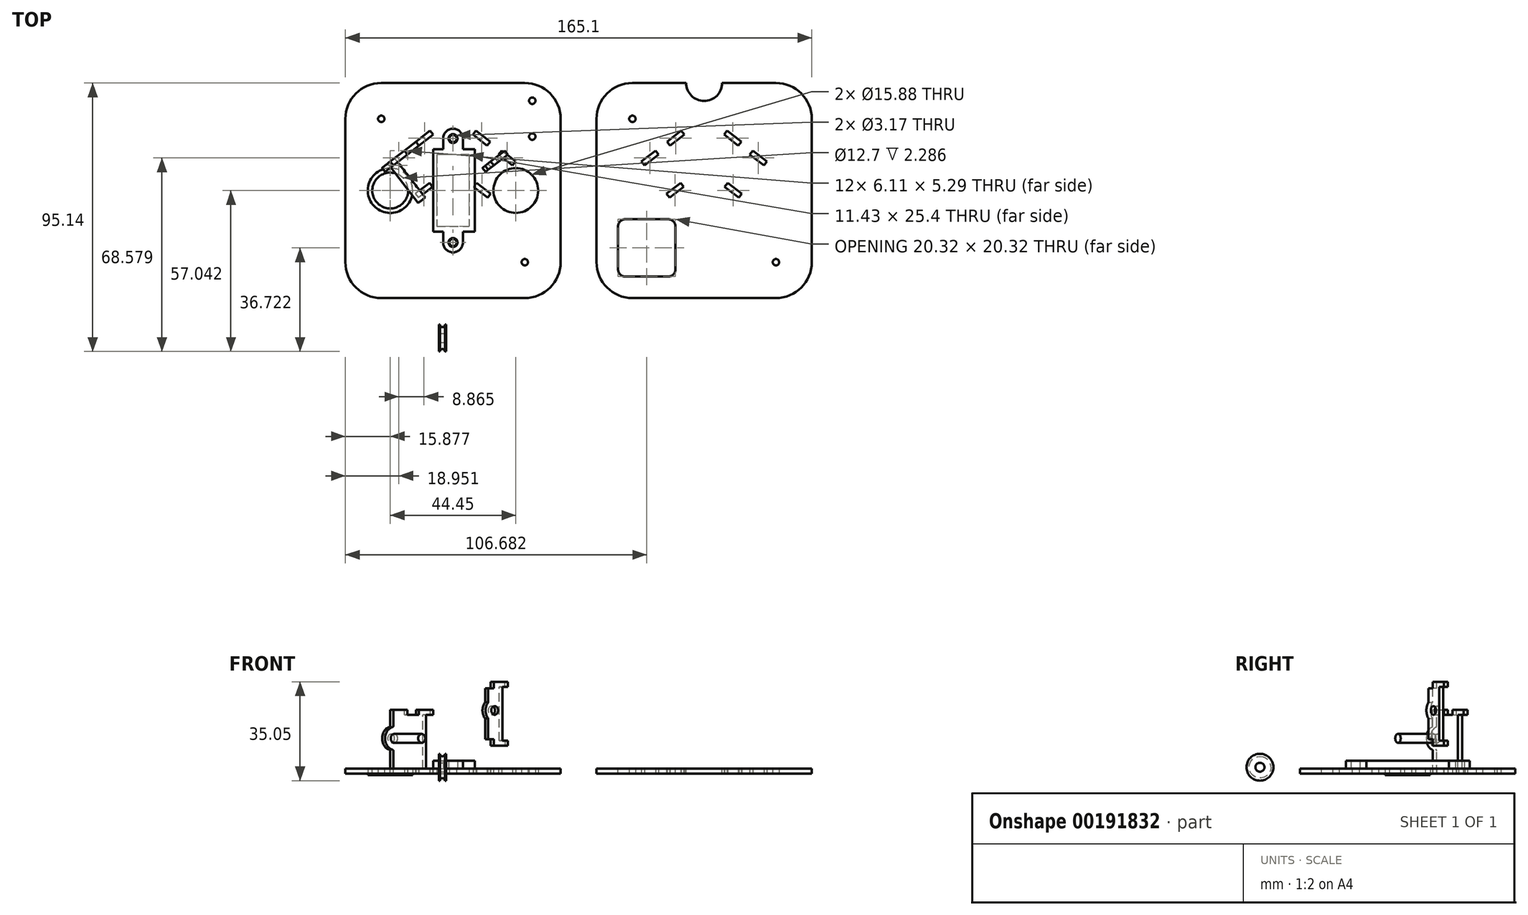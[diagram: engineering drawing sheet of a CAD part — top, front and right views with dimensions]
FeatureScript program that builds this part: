
annotation { "Feature Type Name" : "Feature", "Feature Type Description" : "" }
export const myFeature = defineFeature(function(context is Context, id is Id, definition is map)
    precondition{}
    {
        {
            var Q0;
            Q0=qCreatedBy(makeId("Top.planeOp"),FACE);
            var sketch = newSketch(context, id + "F0", { "sketchPlane" : qUnion([Q0])});
            skLineSegment(sketch, "E0.bottom", {"start": v(-22.88, 61.32) * mm, "end": v(27.92, 61.32) * mm});
            skLineSegment(sketch, "E0.top", {"start": v(-22.88, -14.88) * mm, "end": v(27.92, -14.88) * mm});
            skLineSegment(sketch, "E0.left", {"start": v(-35.58, 48.62) * mm, "end": v(-35.58, -2.18) * mm});
            skLineSegment(sketch, "E0.right", {"start": v(40.62, 48.62) * mm, "end": v(40.62, -2.18) * mm});
            skLineSegment(sketch, "E1", {"start": v(-35.58, 23.22) * mm, "end": v(-3.04, 23.22) * mm, "construction": true});
            skLineSegment(sketch, "E2", {"start": v(2.52, 61.32) * mm, "end": v(2.52, 35.92) * mm, "construction": true});
            skCircle(sketch, "E3", {"center": v(-19.7, 23.22) * mm, "radius": 7.94 * mm});
            skCircle(sketch, "E4.MirrorC", {"center": v(24.75, 23.22) * mm, "radius": 7.94 * mm});
            skLineSegment(sketch, "E5.left", {"start": v(-35.58, 25.46) * mm, "end": v(-35.58, 23.18) * mm});
            skLineSegment(sketch, "E5.right", {"start": v(40.62, 24.72) * mm, "end": v(40.62, 22.44) * mm});
            skPoint(sketch, "E6.visualSharp", {"position": v(-35.58, -14.88) * mm});
            skArc(sketch, "E6.filletArc", {"start": v(-35.58, -2.18) * mm, "mid": v(-31.86, -11.16) * mm, "end": v(-22.88, -14.88) * mm});
            skPoint(sketch, "E7.visualSharp", {"position": v(40.62, -14.88) * mm});
            skArc(sketch, "E7.filletArc", {"start": v(27.92, -14.88) * mm, "mid": v(36.9, -11.16) * mm, "end": v(40.62, -2.18) * mm});
            skPoint(sketch, "E8.visualSharp", {"position": v(40.62, 61.32) * mm});
            skArc(sketch, "E8.filletArc", {"start": v(40.62, 48.62) * mm, "mid": v(36.9, 57.6) * mm, "end": v(27.92, 61.32) * mm});
            skPoint(sketch, "E9.visualSharp", {"position": v(-35.58, 61.32) * mm});
            skArc(sketch, "E9.filletArc", {"start": v(-22.88, 61.32) * mm, "mid": v(-31.86, 57.6) * mm, "end": v(-35.58, 48.62) * mm});
            skLineSegment(sketch, "E10.top", {"start": v(2.52, 35.92) * mm, "end": v(-3.2, 35.92) * mm});
            skLineSegment(sketch, "E11.trimOffspring", {"start": v(8.09, 23.22) * mm, "end": v(40.62, 23.22) * mm, "construction": true});
            skLineSegment(sketch, "E12.trimOffspring", {"start": v(2.52, 10.52) * mm, "end": v(2.52, -14.88) * mm, "construction": true});
            skLineSegment(sketch, "E13.MirrorCS", {"start": v(2.52, 10.52) * mm, "end": v(-3.2, 10.52) * mm});
            skLineSegment(sketch, "E14.MirrorCS", {"start": v(2.52, 10.52) * mm, "end": v(8.24, 10.52) * mm});
            skLineSegment(sketch, "E15.MirrorCS", {"start": v(2.52, 35.92) * mm, "end": v(8.24, 35.92) * mm});
            skLineSegment(sketch, "E16.bottom", {"start": v(-3.2, 35.92) * mm, "end": v(3.3, 35.92) * mm});
            skLineSegment(sketch, "E16.top", {"start": v(-3.2, 10.52) * mm, "end": v(2.52, 10.52) * mm});
            skLineSegment(sketch, "E16.left", {"start": v(-3.2, 35.92) * mm, "end": v(-3.2, 10.52) * mm});
            skPoint(sketch, "E16.right.start.orphan", {"position": v(2.52, 23.22) * mm});
            skCircle(sketch, "E17", {"center": v(2.52, 41.64) * mm, "radius": 1.27 * mm});
            skCircle(sketch, "E18.MirrorC", {"center": v(2.52, 4.8) * mm, "radius": 1.27 * mm});
            skLineSegment(sketch, "E19.MirrorCS", {"start": v(8.24, 35.92) * mm, "end": v(8.24, 10.52) * mm});
            skLineSegment(sketch, "E20", {"start": v(-13.43, 28.08) * mm, "end": v(3.77, 41.4) * mm, "construction": true});
            skLineSegment(sketch, "E21.0", {"start": v(-12.05, 21.12) * mm, "end": v(-3.2, 27.98) * mm, "construction": true});
            skLineSegment(sketch, "E22", {"start": v(-13.57, 36) * mm, "end": v(-14.66, 37.4) * mm});
            skLineSegment(sketch, "E23", {"start": v(-14.66, 37.4) * mm, "end": v(-19.68, 33.52) * mm});
            skLineSegment(sketch, "E24", {"start": v(-10.63, 36.35) * mm, "end": v(-7.68, 32.53) * mm, "construction": true});
            skLineSegment(sketch, "E25", {"start": v(-13.57, 36) * mm, "end": v(-18.6, 32.11) * mm});
            skLineSegment(sketch, "E26", {"start": v(-18.6, 32.11) * mm, "end": v(-19.68, 33.52) * mm});
            skLineSegment(sketch, "E27.MirrorCS", {"start": v(-9.56, 39.11) * mm, "end": v(-10.65, 40.52) * mm});
            skLineSegment(sketch, "E28.MirrorCS", {"start": v(-9.56, 39.11) * mm, "end": v(-4.54, 43) * mm});
            skLineSegment(sketch, "E29.MirrorCS", {"start": v(-10.65, 40.52) * mm, "end": v(-5.63, 44.4) * mm});
            skLineSegment(sketch, "E30.MirrorCS", {"start": v(-4.54, 43) * mm, "end": v(-5.63, 44.4) * mm});
            skLineSegment(sketch, "E31.MirrorCS", {"start": v(-5.8, 25.96) * mm, "end": v(-10.82, 22.07) * mm});
            skLineSegment(sketch, "E32.MirrorCS", {"start": v(-4.7, 24.55) * mm, "end": v(-9.73, 20.67) * mm});
            skLineSegment(sketch, "E33.MirrorCS", {"start": v(-10.82, 22.07) * mm, "end": v(-9.73, 20.67) * mm});
            skLineSegment(sketch, "E34.MirrorCS", {"start": v(-5.8, 25.96) * mm, "end": v(-4.7, 24.55) * mm});
            skLineSegment(sketch, "E35.MirrorCS", {"start": v(18.62, 36) * mm, "end": v(23.64, 32.11) * mm});
            skLineSegment(sketch, "E36.MirrorCS", {"start": v(23.64, 32.11) * mm, "end": v(24.73, 33.52) * mm});
            skLineSegment(sketch, "E37.MirrorCS", {"start": v(19.7, 37.4) * mm, "end": v(24.73, 33.52) * mm});
            skLineSegment(sketch, "E38.MirrorCS", {"start": v(18.62, 36) * mm, "end": v(19.7, 37.4) * mm});
            skLineSegment(sketch, "E39.MirrorCS", {"start": v(9.75, 24.55) * mm, "end": v(14.77, 20.67) * mm});
            skLineSegment(sketch, "E40.MirrorCS", {"start": v(10.84, 25.96) * mm, "end": v(9.75, 24.55) * mm});
            skLineSegment(sketch, "E41.MirrorCS", {"start": v(15.86, 22.07) * mm, "end": v(14.77, 20.67) * mm});
            skLineSegment(sketch, "E42.MirrorCS", {"start": v(17.1, 21.12) * mm, "end": v(8.24, 27.98) * mm, "construction": true});
            skLineSegment(sketch, "E43.MirrorCS", {"start": v(14.6, 39.11) * mm, "end": v(9.58, 43) * mm});
            skLineSegment(sketch, "E44.MirrorCS", {"start": v(9.58, 43) * mm, "end": v(10.67, 44.4) * mm});
            skLineSegment(sketch, "E45.MirrorCS", {"start": v(14.6, 39.11) * mm, "end": v(15.7, 40.52) * mm});
            skLineSegment(sketch, "E46.MirrorCS", {"start": v(15.7, 40.52) * mm, "end": v(10.67, 44.4) * mm});
            skLineSegment(sketch, "E47", {"start": v(10.84, 25.96) * mm, "end": v(15.86, 22.07) * mm});
            skLineSegment(sketch, "E48", {"start": v(12.1, 41.05) * mm, "end": v(13.18, 42.46) * mm, "construction": true});
            skCircle(sketch, "E49", {"center": v(30.58, 42.33) * mm, "radius": 1.14 * mm});
            skCircle(sketch, "E50", {"center": v(30.58, 55.03) * mm, "radius": 1.14 * mm});
            skCircle(sketch, "E51", {"center": v(27.92, -2.18) * mm, "radius": 1.13 * mm});
            skCircle(sketch, "E52", {"center": v(-22.88, 48.62) * mm, "radius": 1.14 * mm});
            skSolve(sketch);
        }
        {
            var Q0;
            Q0=makeQuery(id+"F0.imprint","IMPRINT",FACE,{"disambiguationData":[TD([[makeQuery(id+"F0.imprint","IMPRINT",EDGE,{"derivedFrom":sQuery(id+"F0.wireOp",EDGE,"E0.bottom")}),-1.0]])]});
            extrude(context, id + "F1", {"entities" : qUnion([Q0]), "depth" : 1.78 * mm});
        }
        {
            var Q0;
            Q0=makeQuery(id+"F1.opExtrude","SWEPT_FACE",FACE,{"disambiguationData":[OSD([sQuery(id+"F0.wireOp",EDGE,"E23")])]});
            var sketch = newSketch(context, id + "F2", { "sketchPlane" : qUnion([Q0])});
            skLineSegment(sketch, "E53.top", {"start": v(16.4, 20.83) * mm, "end": v(16.4, 20.83) * mm});
            skCircle(sketch, "E54", {"center": v(5.34, 12.45) * mm, "radius": 1.52 * mm});
            skLineSegment(sketch, "E55", {"start": v(4.96, 2.29) * mm, "end": v(4.96, 7.96) * mm});
            skPoint(sketch, "E53.left.start.orphan", {"position": v(-28.95, 2.29) * mm});
            skPoint(sketch, "E56.orphan", {"position": v(-15.62, 20.83) * mm});
            skPoint(sketch, "E53.right.end.orphan", {"position": v(60.58, 20.83) * mm});
            skPoint(sketch, "E53.right.start.orphan", {"position": v(73.92, 2.29) * mm});
            skLineSegment(sketch, "E57", {"start": v(5.27, 11.3) * mm, "end": v(13.84, 11.3) * mm, "construction": true});
            skLineSegment(sketch, "E58.MirrorCS", {"start": v(4.96, 22.6) * mm, "end": v(11.31, 22.6) * mm});
            skLineSegment(sketch, "E59.MirrorCS", {"start": v(11.31, 20.83) * mm, "end": v(11.31, 22.6) * mm});
            skArc(sketch, "E60.0", {"start": v(4.55, 16.43) * mm, "mid": v(1.28, 12.45) * mm, "end": v(4.55, 8.46) * mm});
            skPoint(sketch, "E61.visualSharp", {"position": v(4.96, 16.5) * mm});
            skArc(sketch, "E61.filletArc", {"start": v(4.55, 16.43) * mm, "mid": v(4.85, 16.6) * mm, "end": v(4.96, 16.93) * mm});
            skPoint(sketch, "E62.visualSharp", {"position": v(4.96, 8.4) * mm});
            skArc(sketch, "E62.filletArc", {"start": v(4.96, 7.96) * mm, "mid": v(4.85, 8.28) * mm, "end": v(4.55, 8.46) * mm});
            skLineSegment(sketch, "E63.MirrorCS", {"start": v(11.31, 20.83) * mm, "end": v(16.4, 20.83) * mm});
            skPoint(sketch, "E64.top.start.orphan", {"position": v(22.48, 6.1) * mm});
            skLineSegment(sketch, "E65", {"start": v(11.31, 1.78) * mm, "end": v(16.4, 1.78) * mm});
            skLineSegment(sketch, "E66.top", {"start": v(22.74, 0) * mm, "end": v(16.4, 0) * mm});
            skLineSegment(sketch, "E66.right", {"start": v(16.4, 1.78) * mm, "end": v(16.4, 0) * mm});
            skLineSegment(sketch, "E67.MirrorCS", {"start": v(22.74, 22.6) * mm, "end": v(16.4, 22.6) * mm});
            skLineSegment(sketch, "E68.MirrorCS", {"start": v(16.4, 20.83) * mm, "end": v(16.4, 22.6) * mm});
            skLineSegment(sketch, "E69.top", {"start": v(11.31, 0) * mm, "end": v(4.96, 0) * mm});
            skLineSegment(sketch, "E69.left", {"start": v(11.31, 1.78) * mm, "end": v(11.31, 0) * mm});
            skLineSegment(sketch, "E69.right", {"start": v(4.96, 2.29) * mm, "end": v(4.96, 0) * mm});
            skLineSegment(sketch, "E70", {"start": v(4.96, 16.93) * mm, "end": v(4.96, 22.6) * mm});
            skLineSegment(sketch, "E71", {"start": v(22.74, 22.6) * mm, "end": v(22.74, 20.83) * mm});
            skLineSegment(sketch, "E72.bottom", {"start": v(22.74, 1.78) * mm, "end": v(19.57, 1.78) * mm});
            skLineSegment(sketch, "E72.top", {"start": v(22.74, 20.83) * mm, "end": v(19.57, 20.83) * mm});
            skLineSegment(sketch, "E72.right", {"start": v(19.57, 1.78) * mm, "end": v(19.57, 20.83) * mm});
            skLineSegment(sketch, "E73.trimOffspring", {"start": v(22.74, 1.78) * mm, "end": v(22.74, 0) * mm});
            skSolve(sketch);
        }
        {
            var Q0;
            Q0=makeQuery(id+"F2.imprint","IMPRINT",FACE,{"disambiguationData":[TD([[makeQuery(id+"F2.imprint","IMPRINT",EDGE,{"derivedFrom":sQuery(id+"F2.wireOp",EDGE,"E54")}),-1.0]])]});
            var Q1;
            Q1=makeQuery(id+"F2.imprint","IMPRINT",FACE,{"disambiguationData":[TD([[makeQuery(id+"F2.imprint","IMPRINT",EDGE,{"derivedFrom":sQuery(id+"F2.wireOp",EDGE,"E69.top")}),-1.0]])]});
            extrude(context, id + "F3", {"entities" : qUnion([Q0, Q1]), "depth" : 1.78 * mm});
        }
        {
            var Q0;
            Q0=makeQuery(id+"F3.opExtrude","SWEPT_BODY",BODY,{"disambiguationData":[OSD([sQuery(id+"F2.wireOp",EDGE,"E53.bottom"),sQuery(id+"F2.wireOp",EDGE,"E53.top"),sQuery(id+"F2.wireOp",EDGE,"E54"),sQuery(id+"F2.wireOp",EDGE,"39a69e0f-4cb4-4542-a178-ce5a3710d4660.MirrorCS"),sQuery(id+"F2.wireOp",EDGE,"5af08400-f977-49c8-b0c8-0518a07f6a520.MirrorCS"),sQuery(id+"F2.wireOp",EDGE,"84274afa-9e7b-4732-9adf-5b7f6b23458d0.MirrorCS"),sQuery(id+"F2.wireOp",EDGE,"E55"),sQuery(id+"F2.wireOp",EDGE,"e57e3ef5-8313-4936-b405-59ef127ed5260.MirrorCS"),sQuery(id+"F2.wireOp",EDGE,"d303f1ce-a37b-40ea-9413-96a8a4c887890.MirrorC"),sQuery(id+"F2.wireOp",EDGE,"Hnc1nS2l-cVDs-HAgH-h4le-MnPWrZNVOkKI.top"),sQuery(id+"F2.wireOp",EDGE,"Hnc1nS2l-cVDs-HAgH-h4le-MnPWrZNVOkKI.left"),sQuery(id+"F2.wireOp",EDGE,"Hnc1nS2l-cVDs-HAgH-h4le-MnPWrZNVOkKI.right"),sQuery(id+"F2.wireOp",EDGE,"d3e6619f-e4b7-4664-bd97-2753edbc48ab0.MirrorCS"),sQuery(id+"F2.wireOp",EDGE,"cd9f6806-109e-4446-bf17-cb16760e91a50.MirrorCS"),sQuery(id+"F2.wireOp",EDGE,"0c942e14-5766-4280-9eae-b5e6824674920.MirrorCS"),sQuery(id+"F2.wireOp",EDGE,"PotOPIpM-QwAl-Cd0Z-i22J-7vAqHJB9KxQS.top"),sQuery(id+"F2.wireOp",EDGE,"PotOPIpM-QwAl-Cd0Z-i22J-7vAqHJB9KxQS.left"),sQuery(id+"F2.wireOp",EDGE,"PotOPIpM-QwAl-Cd0Z-i22J-7vAqHJB9KxQS.right")])]});
            transform(context, id + "F4", {"entities" : qUnion([Q0]), "transformType" : TransformType.TRANSLATION_3D, "dx" : 0 * mm, "dy" : -13.97 * mm, "dz" : 0 * mm, "makeCopy" : true});
        }
        {
            var Q0;
            Q0=qCreatedBy(makeId("Top.planeOp"),FACE);
            var sketch = newSketch(context, id + "F5", { "sketchPlane" : qUnion([Q0])});
            skLineSegment(sketch, "E74.bottom", {"start": v(-11.14, -35.94) * mm, "end": v(-8.6, -35.94) * mm});
            skLineSegment(sketch, "E74.top", {"start": v(-11.14, -31.18) * mm, "end": v(-10.76, -31.18) * mm});
            skLineSegment(sketch, "E74.left", {"start": v(-11.14, -35.94) * mm, "end": v(-11.14, -31.18) * mm});
            skLineSegment(sketch, "E74.right", {"start": v(-8.6, -35.94) * mm, "end": v(-8.6, -31.18) * mm});
            skArc(sketch, "E75", {"start": v(-10.76, -31.18) * mm, "mid": v(-9.87, -32.07) * mm, "end": v(-8.98, -31.18) * mm});
            skLineSegment(sketch, "E76.trimOffspring", {"start": v(-8.98, -31.18) * mm, "end": v(-8.6, -31.18) * mm});
            skSolve(sketch);
        }
        {
            var Q0;
            Q0 = qSketchRegion(id + "F5", true);
            var Q1;
            Q1=sQuery(id+"F5.wireOp",EDGE,"E74.bottom");
            revolve(context, id + "F6", {"entities" : qUnion([Q0]), "axis" : qUnion([Q1]), "revolveType" : RevolveType.FULL});
        }
        {
            var Q0;
            Q0=makeQuery(id+"F6.opRevolve","SWEPT_FACE",FACE,{"disambiguationData":[OSD([sQuery(id+"F5.wireOp",EDGE,"E74.right")])]});
            var sketch = newSketch(context, id + "F7", { "sketchPlane" : qUnion([Q0])});
            skCircle(sketch, "E77", {"center": v(-35.94, 0) * mm, "radius": 1.59 * mm});
            skSolve(sketch);
        }
        {
            var Q0;
            Q0 = qSketchRegion(id + "F7", true);
            extrude(context, id + "F8", {"entities" : qUnion([Q0]), "operationType" : NewBodyOperationType.REMOVE, "endBound" : BoundingType.THROUGH_ALL, "oppositeDirection" : true, "depth" : 25.4 * mm});
        }
        {
            var Q0;
            Q0=makeQuery(id+"F6.opRevolve","SWEPT_BODY",BODY,{"disambiguationData":[OSD([sQuery(id+"F5.wireOp",EDGE,"E74.bottom"),sQuery(id+"F5.wireOp",EDGE,"E74.top"),sQuery(id+"F5.wireOp",EDGE,"E74.left"),sQuery(id+"F5.wireOp",EDGE,"E74.right"),sQuery(id+"F5.wireOp",EDGE,"E75"),sQuery(id+"F5.wireOp",EDGE,"E76.trimOffspring")])]});
            transform(context, id + "F9", {"entities" : qUnion([Q0]), "transformType" : TransformType.TRANSLATION_3D, "dx" : 8.64 * mm, "dy" : 6.88 * mm, "dz" : -0.32 * mm, "makeCopy" : false});
        }
        {
            var Q0;
            Q0=makeQuery(id+"F6.opRevolve","SWEPT_BODY",BODY,{"disambiguationData":[OSD([sQuery(id+"F5.wireOp",EDGE,"E74.bottom"),sQuery(id+"F5.wireOp",EDGE,"E74.top"),sQuery(id+"F5.wireOp",EDGE,"E74.left"),sQuery(id+"F5.wireOp",EDGE,"E74.right"),sQuery(id+"F5.wireOp",EDGE,"E75"),sQuery(id+"F5.wireOp",EDGE,"E76.trimOffspring")])]});
            transform(context, id + "F10", {"entities" : qUnion([Q0]), "transformType" : TransformType.TRANSLATION_3D, "dx" : 33.53 * mm, "dy" : 0 * mm, "dz" : 0 * mm, "makeCopy" : true});
        }
        {
            var Q0;
            Q0=makeQuery(id+"F4.opPattern","COPY",BODY,{"derivedFrom":makeQuery(id+"F3.opExtrude","SWEPT_BODY",BODY,{"disambiguationData":[OSD([sQuery(id+"F2.wireOp",EDGE,"E53.bottom"),sQuery(id+"F2.wireOp",EDGE,"E53.top"),sQuery(id+"F2.wireOp",EDGE,"E54"),sQuery(id+"F2.wireOp",EDGE,"39a69e0f-4cb4-4542-a178-ce5a3710d4660.MirrorCS"),sQuery(id+"F2.wireOp",EDGE,"5af08400-f977-49c8-b0c8-0518a07f6a520.MirrorCS"),sQuery(id+"F2.wireOp",EDGE,"84274afa-9e7b-4732-9adf-5b7f6b23458d0.MirrorCS"),sQuery(id+"F2.wireOp",EDGE,"E55"),sQuery(id+"F2.wireOp",EDGE,"e57e3ef5-8313-4936-b405-59ef127ed5260.MirrorCS"),sQuery(id+"F2.wireOp",EDGE,"d303f1ce-a37b-40ea-9413-96a8a4c887890.MirrorC"),sQuery(id+"F2.wireOp",EDGE,"Hnc1nS2l-cVDs-HAgH-h4le-MnPWrZNVOkKI.top"),sQuery(id+"F2.wireOp",EDGE,"Hnc1nS2l-cVDs-HAgH-h4le-MnPWrZNVOkKI.left"),sQuery(id+"F2.wireOp",EDGE,"Hnc1nS2l-cVDs-HAgH-h4le-MnPWrZNVOkKI.right"),sQuery(id+"F2.wireOp",EDGE,"d3e6619f-e4b7-4664-bd97-2753edbc48ab0.MirrorCS"),sQuery(id+"F2.wireOp",EDGE,"cd9f6806-109e-4446-bf17-cb16760e91a50.MirrorCS"),sQuery(id+"F2.wireOp",EDGE,"0c942e14-5766-4280-9eae-b5e6824674920.MirrorCS"),sQuery(id+"F2.wireOp",EDGE,"PotOPIpM-QwAl-Cd0Z-i22J-7vAqHJB9KxQS.top"),sQuery(id+"F2.wireOp",EDGE,"PotOPIpM-QwAl-Cd0Z-i22J-7vAqHJB9KxQS.left"),sQuery(id+"F2.wireOp",EDGE,"PotOPIpM-QwAl-Cd0Z-i22J-7vAqHJB9KxQS.right")])]}),"instanceName":"1"});
            var Q1;
            Q1=makeQuery(id+"F5I5v5MRCHO6jwp_3.opPattern","COPY",BODY,{"derivedFrom":makeQuery(id+"FqVhxczo7vmOwjE_2.opExtrude","SWEPT_BODY",BODY,{"disambiguationData":[OSD([sQuery(id+"Ffx07k7tmxWMfFj_2.wireOp",EDGE,"6cq6P109-h6eB-oaLu-sk0c-LIsEAzt6sABo")])]}),"instanceName":"1"});
            deleteBodies(context, id + "F11", {"entities" : qUnion([Q0, Q1])});
        }
        {
            var Q0;
            Q0=makeQuery(id+"F10.opPattern","COPY",BODY,{"derivedFrom":makeQuery(id+"F6.opRevolve","SWEPT_BODY",BODY,{"disambiguationData":[OSD([sQuery(id+"F5.wireOp",EDGE,"E74.bottom"),sQuery(id+"F5.wireOp",EDGE,"E74.top"),sQuery(id+"F5.wireOp",EDGE,"E74.left"),sQuery(id+"F5.wireOp",EDGE,"E74.right"),sQuery(id+"F5.wireOp",EDGE,"E75"),sQuery(id+"F5.wireOp",EDGE,"E76.trimOffspring")])]}),"instanceName":"1"});
            deleteBodies(context, id + "F12", {"entities" : qUnion([Q0])});
        }
        {
            var Q0;
            Q0=makeQuery(id+"F6.opRevolve","SWEPT_BODY",BODY,{"disambiguationData":[OSD([sQuery(id+"F5.wireOp",EDGE,"E74.bottom"),sQuery(id+"F5.wireOp",EDGE,"E74.top"),sQuery(id+"F5.wireOp",EDGE,"E74.left"),sQuery(id+"F5.wireOp",EDGE,"E74.right"),sQuery(id+"F5.wireOp",EDGE,"E75"),sQuery(id+"F5.wireOp",EDGE,"E76.trimOffspring")])]});
            transform(context, id + "F13", {"entities" : qUnion([Q0]), "transformType" : TransformType.TRANSLATION_3D, "dx" : 0 * mm, "dy" : 0 * mm, "dz" : 2.54 * mm, "makeCopy" : false});
        }
        {
            var Q0;
            Q0=makeQuery(id+"F1.opExtrude","CAP_FACE",FACE,{"disambiguationData":[OSD([sQuery(id+"F0.wireOp",EDGE,"E0.bottom"),sQuery(id+"F0.wireOp",EDGE,"E0.top"),sQuery(id+"F0.wireOp",EDGE,"E0.left"),sQuery(id+"F0.wireOp",EDGE,"E0.right"),sQuery(id+"F0.wireOp",EDGE,"E3"),sQuery(id+"F0.wireOp",EDGE,"E4.MirrorC"),sQuery(id+"F0.wireOp",EDGE,"E5.left"),sQuery(id+"F0.wireOp",EDGE,"E5.right"),sQuery(id+"F0.wireOp",EDGE,"1d3f4JpI-8B3J-cx4F-wrh8-YEHR3C14XcvI.bottom"),sQuery(id+"F0.wireOp",EDGE,"1d3f4JpI-8B3J-cx4F-wrh8-YEHR3C14XcvI.top"),sQuery(id+"F0.wireOp",EDGE,"1d3f4JpI-8B3J-cx4F-wrh8-YEHR3C14XcvI.left"),sQuery(id+"F0.wireOp",EDGE,"1d3f4JpI-8B3J-cx4F-wrh8-YEHR3C14XcvI.right"),sQuery(id+"F0.wireOp",EDGE,"ded24c36-2829-4a26-ae88-f7eb7b782ba40.MirrorCS"),sQuery(id+"F0.wireOp",EDGE,"0885069f-9e6d-484d-b19d-ad6ea1b2afb20.MirrorCS"),sQuery(id+"F0.wireOp",EDGE,"d2e7fe8c-65ad-4f29-82e6-2e3cbba0d0cb0.MirrorCS"),sQuery(id+"F0.wireOp",EDGE,"fc1c7216-331c-41ae-9cee-ffb66b4a45bf0.MirrorCS"),sQuery(id+"F0.wireOp",EDGE,"71281703-b980-4b41-ad92-6ab3323842a52.MirrorCS"),sQuery(id+"F0.wireOp",EDGE,"71281703-b980-4b41-ad92-6ab3323842a53.MirrorCS"),sQuery(id+"F0.wireOp",EDGE,"71281703-b980-4b41-ad92-6ab3323842a54.MirrorCS"),sQuery(id+"F0.wireOp",EDGE,"71281703-b980-4b41-ad92-6ab3323842a55.MirrorCS"),sQuery(id+"F0.wireOp",EDGE,"86d47684-7b3e-49bb-ae71-ea5330f57f1f0.MirrorCS"),sQuery(id+"F0.wireOp",EDGE,"86d47684-7b3e-49bb-ae71-ea5330f57f1f1.MirrorCS"),sQuery(id+"F0.wireOp",EDGE,"86d47684-7b3e-49bb-ae71-ea5330f57f1f2.MirrorCS"),sQuery(id+"F0.wireOp",EDGE,"86d47684-7b3e-49bb-ae71-ea5330f57f1f3.MirrorCS"),sQuery(id+"F0.wireOp",EDGE,"E6.filletArc"),sQuery(id+"F0.wireOp",EDGE,"E7.filletArc"),sQuery(id+"F0.wireOp",EDGE,"E8.filletArc"),sQuery(id+"F0.wireOp",EDGE,"E9.filletArc")])],"isStart":false});
            var sketch = newSketch(context, id + "F14", { "sketchPlane" : qUnion([Q0])});
            skCircle(sketch, "E78", {"center": v(-19.7, 23.22) * mm, "radius": 7.94 * mm});
            skCircle(sketch, "E79", {"center": v(-19.7, 23.22) * mm, "radius": 6.35 * mm});
            skSolve(sketch);
        }
        {
            var Q0;
            Q0 = qSketchRegion(id + "F14", true);
            extrude(context, id + "F15", {"entities" : qUnion([Q0]), "oppositeDirection" : true, "depth" : 2.3 * mm});
        }
        {
            var Q0;
            Q0=makeQuery(id+"F1.opExtrude","CAP_FACE",FACE,{"disambiguationData":[OSD([sQuery(id+"F0.wireOp",EDGE,"E0.bottom"),sQuery(id+"F0.wireOp",EDGE,"E0.top"),sQuery(id+"F0.wireOp",EDGE,"E0.left"),sQuery(id+"F0.wireOp",EDGE,"E0.right"),sQuery(id+"F0.wireOp",EDGE,"E3"),sQuery(id+"F0.wireOp",EDGE,"E4.MirrorC"),sQuery(id+"F0.wireOp",EDGE,"E5.left"),sQuery(id+"F0.wireOp",EDGE,"E5.right"),sQuery(id+"F0.wireOp",EDGE,"1d3f4JpI-8B3J-cx4F-wrh8-YEHR3C14XcvI.bottom"),sQuery(id+"F0.wireOp",EDGE,"1d3f4JpI-8B3J-cx4F-wrh8-YEHR3C14XcvI.top"),sQuery(id+"F0.wireOp",EDGE,"1d3f4JpI-8B3J-cx4F-wrh8-YEHR3C14XcvI.left"),sQuery(id+"F0.wireOp",EDGE,"1d3f4JpI-8B3J-cx4F-wrh8-YEHR3C14XcvI.right"),sQuery(id+"F0.wireOp",EDGE,"ded24c36-2829-4a26-ae88-f7eb7b782ba40.MirrorCS"),sQuery(id+"F0.wireOp",EDGE,"0885069f-9e6d-484d-b19d-ad6ea1b2afb20.MirrorCS"),sQuery(id+"F0.wireOp",EDGE,"d2e7fe8c-65ad-4f29-82e6-2e3cbba0d0cb0.MirrorCS"),sQuery(id+"F0.wireOp",EDGE,"fc1c7216-331c-41ae-9cee-ffb66b4a45bf0.MirrorCS"),sQuery(id+"F0.wireOp",EDGE,"71281703-b980-4b41-ad92-6ab3323842a52.MirrorCS"),sQuery(id+"F0.wireOp",EDGE,"71281703-b980-4b41-ad92-6ab3323842a53.MirrorCS"),sQuery(id+"F0.wireOp",EDGE,"71281703-b980-4b41-ad92-6ab3323842a54.MirrorCS"),sQuery(id+"F0.wireOp",EDGE,"71281703-b980-4b41-ad92-6ab3323842a55.MirrorCS"),sQuery(id+"F0.wireOp",EDGE,"86d47684-7b3e-49bb-ae71-ea5330f57f1f0.MirrorCS"),sQuery(id+"F0.wireOp",EDGE,"86d47684-7b3e-49bb-ae71-ea5330f57f1f1.MirrorCS"),sQuery(id+"F0.wireOp",EDGE,"86d47684-7b3e-49bb-ae71-ea5330f57f1f2.MirrorCS"),sQuery(id+"F0.wireOp",EDGE,"86d47684-7b3e-49bb-ae71-ea5330f57f1f3.MirrorCS"),sQuery(id+"F0.wireOp",EDGE,"E6.filletArc"),sQuery(id+"F0.wireOp",EDGE,"E7.filletArc"),sQuery(id+"F0.wireOp",EDGE,"E8.filletArc"),sQuery(id+"F0.wireOp",EDGE,"E9.filletArc"),sQuery(id+"F0.wireOp",EDGE,"E14.MirrorCS"),sQuery(id+"F0.wireOp",EDGE,"E15.MirrorCS"),sQuery(id+"F0.wireOp",EDGE,"E16.bottom"),sQuery(id+"F0.wireOp",EDGE,"E16.top"),sQuery(id+"F0.wireOp",EDGE,"E16.left"),sQuery(id+"F0.wireOp",EDGE,"E17"),sQuery(id+"F0.wireOp",EDGE,"E18.MirrorC"),sQuery(id+"F0.wireOp",EDGE,"E19.MirrorCS")])],"isStart":false});
            var sketch = newSketch(context, id + "F16", { "sketchPlane" : qUnion([Q0])});
            skLineSegment(sketch, "E80.bottom", {"start": v(-4.46, 37.83) * mm, "end": v(-0.97, 37.83) * mm});
            skLineSegment(sketch, "E80.top", {"start": v(-4.46, 8.62) * mm, "end": v(2.52, 8.62) * mm});
            skLineSegment(sketch, "E80.left", {"start": v(-4.46, 37.83) * mm, "end": v(-4.46, 8.62) * mm});
            skLineSegment(sketch, "E80.right", {"start": v(10.3, 37.83) * mm, "end": v(10.3, 8.62) * mm});
            skCircle(sketch, "E81", {"center": v(2.52, 41.64) * mm, "radius": 1.59 * mm});
            skArc(sketch, "E82.0", {"start": v(6.01, 41.64) * mm, "mid": v(2.52, 45.13) * mm, "end": v(-0.97, 41.64) * mm});
            skLineSegment(sketch, "E83", {"start": v(-0.97, 41.64) * mm, "end": v(-0.97, 37.83) * mm});
            skLineSegment(sketch, "E84", {"start": v(6.01, 37.83) * mm, "end": v(6.01, 41.64) * mm});
            skLineSegment(sketch, "E85.trimOffspring", {"start": v(6.01, 37.83) * mm, "end": v(10.3, 37.83) * mm});
            skLineSegment(sketch, "E86", {"start": v(2.52, 41.64) * mm, "end": v(2.52, 4.8) * mm, "construction": true});
            skLineSegment(sketch, "E87", {"start": v(-4.46, 23.22) * mm, "end": v(10.3, 23.22) * mm, "construction": true});
            skLineSegment(sketch, "E88.MirrorCS", {"start": v(-0.97, 4.8) * mm, "end": v(-0.97, 8.62) * mm});
            skLineSegment(sketch, "E89.MirrorCS", {"start": v(6.01, 8.62) * mm, "end": v(6.01, 4.8) * mm});
            skCircle(sketch, "E90.MirrorC", {"center": v(2.52, 4.8) * mm, "radius": 1.59 * mm});
            skArc(sketch, "E91.MirrorCS", {"start": v(6.01, 4.8) * mm, "mid": v(2.52, 1.31) * mm, "end": v(-0.97, 4.8) * mm});
            skLineSegment(sketch, "E92.trimOffspring", {"start": v(6.01, 8.62) * mm, "end": v(10.3, 8.62) * mm});
            skSolve(sketch);
        }
        {
            var Q0;
            Q0 = qSketchRegion(id + "F16", true);
            extrude(context, id + "F17", {"entities" : qUnion([Q0]), "depth" : 2.8 * mm});
        }
        {
            var Q0;
            Q0=qCreatedBy(makeId("Top.planeOp"),FACE);
            var sketch = newSketch(context, id + "F18", { "sketchPlane" : qUnion([Q0])});
            skLineSegment(sketch, "E93.bottom", {"start": v(-61.18, 22.56) * mm, "end": v(-40.86, 22.56) * mm});
            skLineSegment(sketch, "E93.top", {"start": v(-61.18, 2.24) * mm, "end": v(-40.86, 2.24) * mm});
            skLineSegment(sketch, "E93.left", {"start": v(-61.18, 22.56) * mm, "end": v(-61.18, 2.24) * mm});
            skLineSegment(sketch, "E93.right", {"start": v(-40.86, 22.56) * mm, "end": v(-40.86, 2.24) * mm});
            skSolve(sketch);
        }
        {
            var Q0;
            Q0 = qSketchRegion(id + "F18", true);
            extrude(context, id + "F19", {"entities" : qUnion([Q0]), "depth" : 0.76 * mm});
        }
        {
            var Q0;
            Q0=makeQuery(id+"F3.opExtrude","CAP_FACE",FACE,{"disambiguationData":[OSD([sQuery(id+"F2.wireOp",EDGE,"E54"),sQuery(id+"F2.wireOp",EDGE,"E55"),sQuery(id+"F2.wireOp",EDGE,"E58.MirrorCS"),sQuery(id+"F2.wireOp",EDGE,"E59.MirrorCS"),sQuery(id+"F2.wireOp",EDGE,"E60.0"),sQuery(id+"F2.wireOp",EDGE,"E61.filletArc"),sQuery(id+"F2.wireOp",EDGE,"E62.filletArc"),sQuery(id+"F2.wireOp",EDGE,"E63.MirrorCS"),sQuery(id+"F2.wireOp",EDGE,"E65"),sQuery(id+"F2.wireOp",EDGE,"E66.top"),sQuery(id+"F2.wireOp",EDGE,"E66.right"),sQuery(id+"F2.wireOp",EDGE,"E67.MirrorCS"),sQuery(id+"F2.wireOp",EDGE,"E68.MirrorCS"),sQuery(id+"F2.wireOp",EDGE,"E69.top"),sQuery(id+"F2.wireOp",EDGE,"E69.left"),sQuery(id+"F2.wireOp",EDGE,"E69.right"),sQuery(id+"F2.wireOp",EDGE,"E70"),sQuery(id+"F2.wireOp",EDGE,"E71"),sQuery(id+"F2.wireOp",EDGE,"E72.bottom"),sQuery(id+"F2.wireOp",EDGE,"E72.top"),sQuery(id+"F2.wireOp",EDGE,"E72.right"),sQuery(id+"F2.wireOp",EDGE,"E73.trimOffspring")])],"isStart":false});
            var sketch = newSketch(context, id + "F20", { "sketchPlane" : qUnion([Q0])});
            skSolve(sketch);
        }
        {
            var Q0;
            Q0=makeQuery(id+"F19.opExtrude","SWEPT_BODY",BODY,{"disambiguationData":[OSD([sQuery(id+"F18.wireOp",EDGE,"E93.bottom"),sQuery(id+"F18.wireOp",EDGE,"E93.top"),sQuery(id+"F18.wireOp",EDGE,"E93.left"),sQuery(id+"F18.wireOp",EDGE,"E93.right")])]});
            deleteBodies(context, id + "F21", {"entities" : qUnion([Q0])});
        }
        {
            var Q0;
            Q0=makeQuery(id+"F2.imprint","IMPRINT",FACE,{"disambiguationData":[TD([[makeQuery(id+"F2.imprint","IMPRINT",EDGE,{"derivedFrom":sQuery(id+"F2.wireOp",EDGE,"E53.top")}),-1.0]])]});
            var Q1;
            Q1=makeQuery(id+"F1.opExtrude","SWEPT_FACE",FACE,{"disambiguationData":[OSD([sQuery(id+"F0.wireOp",EDGE,"E23")])]});
            extrude(context, id + "F22", {"entities" : qUnion([Q0, Q1]), "depth" : 2.3 * mm});
        }
        {
            var Q0;
            Q0=makeQuery(id+"F22.opExtrude","SWEPT_BODY",BODY,{"disambiguationData":[OSD([sQuery(id+"F0.wireOp",EDGE,"E23"),sQuery(id+"F2.wireOp",EDGE,"E53.top"),sQuery(id+"F2.wireOp",EDGE,"E54"),sQuery(id+"F2.wireOp",EDGE,"E55"),sQuery(id+"F2.wireOp",EDGE,"WHruHp0s-jkxV-5qzF-Qybe-Oz99I8PsOxOz"),sQuery(id+"F2.wireOp",EDGE,"8a088f5d-23f1-4320-8741-7093c85a890b0.MirrorCS"),sQuery(id+"F2.wireOp",EDGE,"fb6294cb-31d4-48fc-97ae-27b581cba4ac0.MirrorCS"),sQuery(id+"F2.wireOp",EDGE,"E58.MirrorCS"),sQuery(id+"F2.wireOp",EDGE,"E59.MirrorCS"),sQuery(id+"F2.wireOp",EDGE,"E60.0"),sQuery(id+"F2.wireOp",EDGE,"cc37b2d1-d642-4a99-835f-9cc889cb6c43.trimOffspring"),sQuery(id+"F2.wireOp",EDGE,"E61.filletArc"),sQuery(id+"F2.wireOp",EDGE,"E62.filletArc"),sQuery(id+"F2.wireOp",EDGE,"E63.MirrorCS"),sQuery(id+"F2.wireOp",EDGE,"E65"),sQuery(id+"F2.wireOp",EDGE,"E66.top"),sQuery(id+"F2.wireOp",EDGE,"E66.left"),sQuery(id+"F2.wireOp",EDGE,"E66.right"),sQuery(id+"F2.wireOp",EDGE,"E67.MirrorCS"),sQuery(id+"F2.wireOp",EDGE,"E68.MirrorCS"),sQuery(id+"F2.wireOp",EDGE,"a5fc17ce-e76f-4f47-bbfe-69127122317b0.MirrorCS"),sQuery(id+"F2.wireOp",EDGE,"78biwzFY-XBJ6-CUMO-rUBM-ugzEQcQVKKgm")])]});
            var Q1;
            Q1=makeQuery(id+"F22.opExtrude","SWEPT_BODY",BODY,{"disambiguationData":[OSD([sQuery(id+"F0.wireOp",EDGE,"E23")])]});
            deleteBodies(context, id + "F23", {"entities" : qUnion([Q0, Q1])});
        }
        {
            var Q0;
            Q0=makeQuery(id+"F3.opExtrude","SWEPT_BODY",BODY,{"disambiguationData":[OSD([sQuery(id+"F2.wireOp",EDGE,"E53.top"),sQuery(id+"F2.wireOp",EDGE,"E54"),sQuery(id+"F2.wireOp",EDGE,"E55"),sQuery(id+"F2.wireOp",EDGE,"WHruHp0s-jkxV-5qzF-Qybe-Oz99I8PsOxOz"),sQuery(id+"F2.wireOp",EDGE,"8a088f5d-23f1-4320-8741-7093c85a890b0.MirrorCS"),sQuery(id+"F2.wireOp",EDGE,"fb6294cb-31d4-48fc-97ae-27b581cba4ac0.MirrorCS"),sQuery(id+"F2.wireOp",EDGE,"E58.MirrorCS"),sQuery(id+"F2.wireOp",EDGE,"E59.MirrorCS"),sQuery(id+"F2.wireOp",EDGE,"E60.0"),sQuery(id+"F2.wireOp",EDGE,"cc37b2d1-d642-4a99-835f-9cc889cb6c43.trimOffspring"),sQuery(id+"F2.wireOp",EDGE,"E61.filletArc"),sQuery(id+"F2.wireOp",EDGE,"E62.filletArc"),sQuery(id+"F2.wireOp",EDGE,"E63.MirrorCS"),sQuery(id+"F2.wireOp",EDGE,"E65"),sQuery(id+"F2.wireOp",EDGE,"E66.top"),sQuery(id+"F2.wireOp",EDGE,"E66.left"),sQuery(id+"F2.wireOp",EDGE,"E66.right"),sQuery(id+"F2.wireOp",EDGE,"E67.MirrorCS"),sQuery(id+"F2.wireOp",EDGE,"E68.MirrorCS"),sQuery(id+"F2.wireOp",EDGE,"a5fc17ce-e76f-4f47-bbfe-69127122317b0.MirrorCS"),sQuery(id+"F2.wireOp",EDGE,"78biwzFY-XBJ6-CUMO-rUBM-ugzEQcQVKKgm"),sQuery(id+"F2.wireOp",EDGE,"E69.top"),sQuery(id+"F2.wireOp",EDGE,"E69.left"),sQuery(id+"F2.wireOp",EDGE,"E69.right")])]});
            transform(context, id + "F24", {"entities" : qUnion([Q0]), "transformType" : TransformType.TRANSLATION_3D, "dx" : 35.56 * mm, "dy" : 0 * mm, "dz" : 9.9 * mm, "makeCopy" : true});
        }
        {
            var Q0;
            Q0=makeQuery(id+"F24.opPattern","COPY",FACE,{"derivedFrom":makeQuery(id+"F3.opExtrude","CAP_FACE",FACE,{"disambiguationData":[OSD([sQuery(id+"F2.wireOp",EDGE,"E53.top"),sQuery(id+"F2.wireOp",EDGE,"E54"),sQuery(id+"F2.wireOp",EDGE,"E55"),sQuery(id+"F2.wireOp",EDGE,"WHruHp0s-jkxV-5qzF-Qybe-Oz99I8PsOxOz"),sQuery(id+"F2.wireOp",EDGE,"8a088f5d-23f1-4320-8741-7093c85a890b0.MirrorCS"),sQuery(id+"F2.wireOp",EDGE,"fb6294cb-31d4-48fc-97ae-27b581cba4ac0.MirrorCS"),sQuery(id+"F2.wireOp",EDGE,"E58.MirrorCS"),sQuery(id+"F2.wireOp",EDGE,"E59.MirrorCS"),sQuery(id+"F2.wireOp",EDGE,"E60.0"),sQuery(id+"F2.wireOp",EDGE,"cc37b2d1-d642-4a99-835f-9cc889cb6c43.trimOffspring"),sQuery(id+"F2.wireOp",EDGE,"E61.filletArc"),sQuery(id+"F2.wireOp",EDGE,"E62.filletArc"),sQuery(id+"F2.wireOp",EDGE,"E63.MirrorCS"),sQuery(id+"F2.wireOp",EDGE,"E65"),sQuery(id+"F2.wireOp",EDGE,"E66.top"),sQuery(id+"F2.wireOp",EDGE,"E66.left"),sQuery(id+"F2.wireOp",EDGE,"E66.right"),sQuery(id+"F2.wireOp",EDGE,"E67.MirrorCS"),sQuery(id+"F2.wireOp",EDGE,"E68.MirrorCS"),sQuery(id+"F2.wireOp",EDGE,"a5fc17ce-e76f-4f47-bbfe-69127122317b0.MirrorCS"),sQuery(id+"F2.wireOp",EDGE,"78biwzFY-XBJ6-CUMO-rUBM-ugzEQcQVKKgm"),sQuery(id+"F2.wireOp",EDGE,"E69.top"),sQuery(id+"F2.wireOp",EDGE,"E69.left"),sQuery(id+"F2.wireOp",EDGE,"E69.right")])],"isStart":false}),"instanceName":"1"});
            var sketch = newSketch(context, id + "F25", { "sketchPlane" : qUnion([Q0])});
            skLineSegment(sketch, "E94.bottom", {"start": v(39.43, 32.51) * mm, "end": v(50.86, 32.51) * mm});
            skLineSegment(sketch, "E94.top", {"start": v(39.43, 9.9) * mm, "end": v(50.86, 9.9) * mm});
            skLineSegment(sketch, "E94.left", {"start": v(39.43, 32.51) * mm, "end": v(39.43, 30.73) * mm});
            skLineSegment(sketch, "E94.right", {"start": v(50.86, 32.51) * mm, "end": v(50.86, 9.9) * mm});
            skLineSegment(sketch, "E95.bottom", {"start": v(39.43, 11.68) * mm, "end": v(36.89, 11.68) * mm});
            skLineSegment(sketch, "E95.top", {"start": v(39.43, 30.73) * mm, "end": v(36.89, 30.73) * mm});
            skLineSegment(sketch, "E95.right", {"start": v(36.89, 11.68) * mm, "end": v(36.89, 30.73) * mm});
            skLineSegment(sketch, "E96.trimOffspring", {"start": v(39.43, 11.68) * mm, "end": v(39.43, 9.9) * mm});
            skSolve(sketch);
        }
        {
            var Q0;
            Q0 = qSketchRegion(id + "F25", true);
            extrude(context, id + "F26", {"entities" : qUnion([Q0]), "operationType" : NewBodyOperationType.REMOVE, "endBound" : BoundingType.THROUGH_ALL, "oppositeDirection" : true, "depth" : 25.4 * mm});
        }
        {
            var Q0;
            Q0=makeQuery(id+"F24.opPattern","COPY",FACE,{"derivedFrom":makeQuery(id+"F3.opExtrude","CAP_FACE",FACE,{"disambiguationData":[OSD([sQuery(id+"F2.wireOp",EDGE,"E54"),sQuery(id+"F2.wireOp",EDGE,"E55"),sQuery(id+"F2.wireOp",EDGE,"E58.MirrorCS"),sQuery(id+"F2.wireOp",EDGE,"E59.MirrorCS"),sQuery(id+"F2.wireOp",EDGE,"E60.0"),sQuery(id+"F2.wireOp",EDGE,"E61.filletArc"),sQuery(id+"F2.wireOp",EDGE,"E62.filletArc"),sQuery(id+"F2.wireOp",EDGE,"E63.MirrorCS"),sQuery(id+"F2.wireOp",EDGE,"E65"),sQuery(id+"F2.wireOp",EDGE,"E66.top"),sQuery(id+"F2.wireOp",EDGE,"E66.right"),sQuery(id+"F2.wireOp",EDGE,"E67.MirrorCS"),sQuery(id+"F2.wireOp",EDGE,"E68.MirrorCS"),sQuery(id+"F2.wireOp",EDGE,"E69.top"),sQuery(id+"F2.wireOp",EDGE,"E69.left"),sQuery(id+"F2.wireOp",EDGE,"E69.right"),sQuery(id+"F2.wireOp",EDGE,"E70"),sQuery(id+"F2.wireOp",EDGE,"E71"),sQuery(id+"F2.wireOp",EDGE,"E72.bottom"),sQuery(id+"F2.wireOp",EDGE,"E72.top"),sQuery(id+"F2.wireOp",EDGE,"E72.right"),sQuery(id+"F2.wireOp",EDGE,"E73.trimOffspring")])],"isStart":false}),"instanceName":"1"});
            var sketch = newSketch(context, id + "F27", { "sketchPlane" : qUnion([Q0])});
            skLineSegment(sketch, "E97.bottom", {"start": v(33.08, 12.2) * mm, "end": v(30.54, 12.2) * mm});
            skLineSegment(sketch, "E97.top", {"start": v(33.08, 19.68) * mm, "end": v(30.54, 19.68) * mm});
            skLineSegment(sketch, "E97.left", {"start": v(33.08, 12.2) * mm, "end": v(33.08, 19.68) * mm});
            skLineSegment(sketch, "E97.right", {"start": v(30.54, 12.2) * mm, "end": v(30.54, 19.68) * mm});
            skLineSegment(sketch, "E98.bottom", {"start": v(33.08, 30.23) * mm, "end": v(30.54, 30.23) * mm});
            skLineSegment(sketch, "E98.top", {"start": v(33.08, 24.27) * mm, "end": v(30.54, 24.27) * mm});
            skLineSegment(sketch, "E98.left", {"start": v(33.08, 30.23) * mm, "end": v(33.08, 24.27) * mm});
            skLineSegment(sketch, "E98.right", {"start": v(30.54, 30.23) * mm, "end": v(30.54, 24.27) * mm});
            skSolve(sketch);
        }
        {
            var Q0;
            Q0=makeQuery(id+"F20.imprint","IMPRINT",FACE,{"disambiguationData":[TD([[makeQuery(id+"F20.imprint","IMPRINT",EDGE,{"derivedFrom":makeQuery(id+"F3.opExtrude","CAP_EDGE",EDGE,{"disambiguationData":[OSD([sQuery(id+"F2.wireOp",EDGE,"E54")])],"isStart":false})}),1.0]])]});
            var sketch = newSketch(context, id + "F28", { "sketchPlane" : qUnion([Q0])});
            skCircle(sketch, "E99", {"center": v(5.34, 12.45) * mm, "radius": 1.57 * mm});
            skSolve(sketch);
        }
        {
            var Q0;
            Q0=makeQuery(id+"F1.opExtrude","SWEPT_BODY",BODY,{"disambiguationData":[OSD([sQuery(id+"F0.wireOp",EDGE,"E0.bottom"),sQuery(id+"F0.wireOp",EDGE,"E0.top"),sQuery(id+"F0.wireOp",EDGE,"E0.left"),sQuery(id+"F0.wireOp",EDGE,"E0.right"),sQuery(id+"F0.wireOp",EDGE,"E3"),sQuery(id+"F0.wireOp",EDGE,"E4.MirrorC"),sQuery(id+"F0.wireOp",EDGE,"E5.left"),sQuery(id+"F0.wireOp",EDGE,"E5.right"),sQuery(id+"F0.wireOp",EDGE,"E6.filletArc"),sQuery(id+"F0.wireOp",EDGE,"E7.filletArc"),sQuery(id+"F0.wireOp",EDGE,"E8.filletArc"),sQuery(id+"F0.wireOp",EDGE,"E9.filletArc"),sQuery(id+"F0.wireOp",EDGE,"E14.MirrorCS"),sQuery(id+"F0.wireOp",EDGE,"E15.MirrorCS"),sQuery(id+"F0.wireOp",EDGE,"E16.bottom"),sQuery(id+"F0.wireOp",EDGE,"E16.top"),sQuery(id+"F0.wireOp",EDGE,"E16.left"),sQuery(id+"F0.wireOp",EDGE,"E17"),sQuery(id+"F0.wireOp",EDGE,"E18.MirrorC"),sQuery(id+"F0.wireOp",EDGE,"E19.MirrorCS"),sQuery(id+"F0.wireOp",EDGE,"E22"),sQuery(id+"F0.wireOp",EDGE,"E23"),sQuery(id+"F0.wireOp",EDGE,"E25"),sQuery(id+"F0.wireOp",EDGE,"E26"),sQuery(id+"F0.wireOp",EDGE,"E27.MirrorCS"),sQuery(id+"F0.wireOp",EDGE,"E28.MirrorCS"),sQuery(id+"F0.wireOp",EDGE,"E29.MirrorCS"),sQuery(id+"F0.wireOp",EDGE,"E30.MirrorCS"),sQuery(id+"F0.wireOp",EDGE,"E31.MirrorCS"),sQuery(id+"F0.wireOp",EDGE,"E32.MirrorCS"),sQuery(id+"F0.wireOp",EDGE,"E33.MirrorCS"),sQuery(id+"F0.wireOp",EDGE,"E34.MirrorCS"),sQuery(id+"F0.wireOp",EDGE,"E35.MirrorCS"),sQuery(id+"F0.wireOp",EDGE,"E36.MirrorCS"),sQuery(id+"F0.wireOp",EDGE,"E37.MirrorCS"),sQuery(id+"F0.wireOp",EDGE,"E38.MirrorCS"),sQuery(id+"F0.wireOp",EDGE,"E39.MirrorCS"),sQuery(id+"F0.wireOp",EDGE,"E40.MirrorCS"),sQuery(id+"F0.wireOp",EDGE,"E41.MirrorCS"),sQuery(id+"F0.wireOp",EDGE,"E43.MirrorCS"),sQuery(id+"F0.wireOp",EDGE,"E44.MirrorCS"),sQuery(id+"F0.wireOp",EDGE,"E45.MirrorCS"),sQuery(id+"F0.wireOp",EDGE,"E46.MirrorCS"),sQuery(id+"F0.wireOp",EDGE,"E47"),sQuery(id+"F0.wireOp",EDGE,"E49"),sQuery(id+"F0.wireOp",EDGE,"E50"),sQuery(id+"F0.wireOp",EDGE,"E51"),sQuery(id+"F0.wireOp",EDGE,"E52")])]});
            transform(context, id + "F29", {"entities" : qUnion([Q0]), "transformType" : TransformType.TRANSLATION_3D, "dx" : 88.9 * mm, "dy" : 0 * mm, "dz" : 0 * mm, "makeCopy" : true});
        }
        {
            var Q0;
            Q0=makeQuery(id+"F29.opPattern","COPY",FACE,{"derivedFrom":makeQuery(id+"F1.opExtrude","CAP_FACE",FACE,{"disambiguationData":[OSD([sQuery(id+"F0.wireOp",EDGE,"E0.bottom"),sQuery(id+"F0.wireOp",EDGE,"E0.top"),sQuery(id+"F0.wireOp",EDGE,"E0.left"),sQuery(id+"F0.wireOp",EDGE,"E0.right"),sQuery(id+"F0.wireOp",EDGE,"E3"),sQuery(id+"F0.wireOp",EDGE,"E4.MirrorC"),sQuery(id+"F0.wireOp",EDGE,"E5.left"),sQuery(id+"F0.wireOp",EDGE,"E5.right"),sQuery(id+"F0.wireOp",EDGE,"E6.filletArc"),sQuery(id+"F0.wireOp",EDGE,"E7.filletArc"),sQuery(id+"F0.wireOp",EDGE,"E8.filletArc"),sQuery(id+"F0.wireOp",EDGE,"E9.filletArc"),sQuery(id+"F0.wireOp",EDGE,"E14.MirrorCS"),sQuery(id+"F0.wireOp",EDGE,"E15.MirrorCS"),sQuery(id+"F0.wireOp",EDGE,"E16.bottom"),sQuery(id+"F0.wireOp",EDGE,"E16.top"),sQuery(id+"F0.wireOp",EDGE,"E16.left"),sQuery(id+"F0.wireOp",EDGE,"E17"),sQuery(id+"F0.wireOp",EDGE,"E18.MirrorC"),sQuery(id+"F0.wireOp",EDGE,"E19.MirrorCS"),sQuery(id+"F0.wireOp",EDGE,"E22"),sQuery(id+"F0.wireOp",EDGE,"E23"),sQuery(id+"F0.wireOp",EDGE,"E25"),sQuery(id+"F0.wireOp",EDGE,"E26"),sQuery(id+"F0.wireOp",EDGE,"E27.MirrorCS"),sQuery(id+"F0.wireOp",EDGE,"E28.MirrorCS"),sQuery(id+"F0.wireOp",EDGE,"E29.MirrorCS"),sQuery(id+"F0.wireOp",EDGE,"E30.MirrorCS"),sQuery(id+"F0.wireOp",EDGE,"E31.MirrorCS"),sQuery(id+"F0.wireOp",EDGE,"E32.MirrorCS"),sQuery(id+"F0.wireOp",EDGE,"E33.MirrorCS"),sQuery(id+"F0.wireOp",EDGE,"E34.MirrorCS"),sQuery(id+"F0.wireOp",EDGE,"E35.MirrorCS"),sQuery(id+"F0.wireOp",EDGE,"E36.MirrorCS"),sQuery(id+"F0.wireOp",EDGE,"E37.MirrorCS"),sQuery(id+"F0.wireOp",EDGE,"E38.MirrorCS"),sQuery(id+"F0.wireOp",EDGE,"E39.MirrorCS"),sQuery(id+"F0.wireOp",EDGE,"E40.MirrorCS"),sQuery(id+"F0.wireOp",EDGE,"E41.MirrorCS"),sQuery(id+"F0.wireOp",EDGE,"E43.MirrorCS"),sQuery(id+"F0.wireOp",EDGE,"E44.MirrorCS"),sQuery(id+"F0.wireOp",EDGE,"E45.MirrorCS"),sQuery(id+"F0.wireOp",EDGE,"E46.MirrorCS"),sQuery(id+"F0.wireOp",EDGE,"E47"),sQuery(id+"F0.wireOp",EDGE,"E49"),sQuery(id+"F0.wireOp",EDGE,"E50"),sQuery(id+"F0.wireOp",EDGE,"E51"),sQuery(id+"F0.wireOp",EDGE,"E52")])],"isStart":false}),"instanceName":"1"});
            var sketch = newSketch(context, id + "F30", { "sketchPlane" : qUnion([Q0])});
            skCircle(sketch, "E100", {"center": v(69.2, 23.22) * mm, "radius": 8.9 * mm});
            skCircle(sketch, "E101", {"center": v(113.65, 23.22) * mm, "radius": 8.68 * mm});
            skLineSegment(sketch, "E102.bottom", {"start": v(97.14, 10.52) * mm, "end": v(85.7, 10.52) * mm});
            skLineSegment(sketch, "E102.top", {"start": v(97.14, 35.92) * mm, "end": v(85.7, 35.92) * mm});
            skLineSegment(sketch, "E102.left", {"start": v(97.14, 10.52) * mm, "end": v(97.14, 35.92) * mm});
            skLineSegment(sketch, "E102.right", {"start": v(85.7, 10.52) * mm, "end": v(85.7, 35.92) * mm});
            skCircle(sketch, "E103", {"center": v(91.42, 41.64) * mm, "radius": 1.38 * mm});
            skCircle(sketch, "E104", {"center": v(119.48, 42.33) * mm, "radius": 2.4 * mm});
            skCircle(sketch, "E105", {"center": v(119.48, 55.03) * mm, "radius": 2.47 * mm});
            skCircle(sketch, "E106", {"center": v(91.42, 4.8) * mm, "radius": 2.96 * mm});
            skSolve(sketch);
        }
        {
            var Q0;
            Q0 = qSketchRegion(id + "F30", true);
            extrude(context, id + "F31", {"entities" : qUnion([Q0]), "operationType" : NewBodyOperationType.ADD, "oppositeDirection" : true, "depth" : 1.78 * mm});
        }
        {
            var Q0;
            Q0=makeQuery(id+"F31.boolean.opBoolean","MERGE",FACE,{"derivedFrom":[makeQuery(id+"F29.opPattern","COPY",FACE,{"derivedFrom":makeQuery(id+"F1.opExtrude","CAP_FACE",FACE,{"disambiguationData":[OSD([sQuery(id+"F0.wireOp",EDGE,"E0.bottom"),sQuery(id+"F0.wireOp",EDGE,"E0.top"),sQuery(id+"F0.wireOp",EDGE,"E0.left"),sQuery(id+"F0.wireOp",EDGE,"E0.right"),sQuery(id+"F0.wireOp",EDGE,"E3"),sQuery(id+"F0.wireOp",EDGE,"E4.MirrorC"),sQuery(id+"F0.wireOp",EDGE,"E5.left"),sQuery(id+"F0.wireOp",EDGE,"E5.right"),sQuery(id+"F0.wireOp",EDGE,"E6.filletArc"),sQuery(id+"F0.wireOp",EDGE,"E7.filletArc"),sQuery(id+"F0.wireOp",EDGE,"E8.filletArc"),sQuery(id+"F0.wireOp",EDGE,"E9.filletArc"),sQuery(id+"F0.wireOp",EDGE,"E14.MirrorCS"),sQuery(id+"F0.wireOp",EDGE,"E15.MirrorCS"),sQuery(id+"F0.wireOp",EDGE,"E16.bottom"),sQuery(id+"F0.wireOp",EDGE,"E16.top"),sQuery(id+"F0.wireOp",EDGE,"E16.left"),sQuery(id+"F0.wireOp",EDGE,"E17"),sQuery(id+"F0.wireOp",EDGE,"E18.MirrorC"),sQuery(id+"F0.wireOp",EDGE,"E19.MirrorCS"),sQuery(id+"F0.wireOp",EDGE,"E22"),sQuery(id+"F0.wireOp",EDGE,"E23"),sQuery(id+"F0.wireOp",EDGE,"E25"),sQuery(id+"F0.wireOp",EDGE,"E26"),sQuery(id+"F0.wireOp",EDGE,"E27.MirrorCS"),sQuery(id+"F0.wireOp",EDGE,"E28.MirrorCS"),sQuery(id+"F0.wireOp",EDGE,"E29.MirrorCS"),sQuery(id+"F0.wireOp",EDGE,"E30.MirrorCS"),sQuery(id+"F0.wireOp",EDGE,"E31.MirrorCS"),sQuery(id+"F0.wireOp",EDGE,"E32.MirrorCS"),sQuery(id+"F0.wireOp",EDGE,"E33.MirrorCS"),sQuery(id+"F0.wireOp",EDGE,"E34.MirrorCS"),sQuery(id+"F0.wireOp",EDGE,"E35.MirrorCS"),sQuery(id+"F0.wireOp",EDGE,"E36.MirrorCS"),sQuery(id+"F0.wireOp",EDGE,"E37.MirrorCS"),sQuery(id+"F0.wireOp",EDGE,"E38.MirrorCS"),sQuery(id+"F0.wireOp",EDGE,"E39.MirrorCS"),sQuery(id+"F0.wireOp",EDGE,"E40.MirrorCS"),sQuery(id+"F0.wireOp",EDGE,"E41.MirrorCS"),sQuery(id+"F0.wireOp",EDGE,"E43.MirrorCS"),sQuery(id+"F0.wireOp",EDGE,"E44.MirrorCS"),sQuery(id+"F0.wireOp",EDGE,"E45.MirrorCS"),sQuery(id+"F0.wireOp",EDGE,"E46.MirrorCS"),sQuery(id+"F0.wireOp",EDGE,"E47"),sQuery(id+"F0.wireOp",EDGE,"E49"),sQuery(id+"F0.wireOp",EDGE,"E50"),sQuery(id+"F0.wireOp",EDGE,"E51"),sQuery(id+"F0.wireOp",EDGE,"E52")])],"isStart":false}),"instanceName":"1"}),makeQuery(id+"F31.opExtrude","CAP_FACE",FACE,{"disambiguationData":[OSD([sQuery(id+"F30.wireOp",EDGE,"E100")])],"isStart":true}),makeQuery(id+"F31.opExtrude","CAP_FACE",FACE,{"disambiguationData":[OSD([sQuery(id+"F30.wireOp",EDGE,"E101")])],"isStart":true}),makeQuery(id+"F31.opExtrude","CAP_FACE",FACE,{"disambiguationData":[OSD([sQuery(id+"F30.wireOp",EDGE,"E102.bottom"),sQuery(id+"F30.wireOp",EDGE,"E102.top"),sQuery(id+"F30.wireOp",EDGE,"E102.left"),sQuery(id+"F30.wireOp",EDGE,"E102.right")])],"isStart":true}),makeQuery(id+"F31.opExtrude","CAP_FACE",FACE,{"disambiguationData":[OSD([sQuery(id+"F30.wireOp",EDGE,"E103")])],"isStart":true}),makeQuery(id+"F31.opExtrude","CAP_FACE",FACE,{"disambiguationData":[OSD([sQuery(id+"F30.wireOp",EDGE,"E104")])],"isStart":true}),makeQuery(id+"F31.opExtrude","CAP_FACE",FACE,{"disambiguationData":[OSD([sQuery(id+"F30.wireOp",EDGE,"E105")])],"isStart":true}),makeQuery(id+"F31.opExtrude","CAP_FACE",FACE,{"disambiguationData":[OSD([sQuery(id+"F30.wireOp",EDGE,"E106")])],"isStart":true})]});
            var sketch = newSketch(context, id + "F32", { "sketchPlane" : qUnion([Q0])});
            skLineSegment(sketch, "E107.bottom", {"start": v(63.48, 13.06) * mm, "end": v(78.72, 13.06) * mm});
            skLineSegment(sketch, "E107.top", {"start": v(63.48, -7.26) * mm, "end": v(78.72, -7.26) * mm});
            skLineSegment(sketch, "E107.left", {"start": v(60.94, 10.52) * mm, "end": v(60.94, -4.72) * mm});
            skLineSegment(sketch, "E107.right", {"start": v(81.26, 10.52) * mm, "end": v(81.26, -4.72) * mm});
            skLineSegment(sketch, "E108", {"start": v(91.42, 61.32) * mm, "end": v(91.42, -14.88) * mm, "construction": true});
            skLineSegment(sketch, "E109", {"start": v(129.52, 23.22) * mm, "end": v(53.32, 23.22) * mm, "construction": true});
            skPoint(sketch, "E110.visualSharp", {"position": v(60.94, 13.06) * mm});
            skArc(sketch, "E110.filletArc", {"start": v(63.48, 13.06) * mm, "mid": v(61.69, 12.32) * mm, "end": v(60.94, 10.52) * mm});
            skPoint(sketch, "E111.visualSharp", {"position": v(81.26, 13.06) * mm});
            skArc(sketch, "E111.filletArc", {"start": v(81.26, 10.52) * mm, "mid": v(80.52, 12.32) * mm, "end": v(78.72, 13.06) * mm});
            skPoint(sketch, "E112.visualSharp", {"position": v(81.26, -7.26) * mm});
            skArc(sketch, "E112.filletArc", {"start": v(78.72, -7.26) * mm, "mid": v(80.52, -6.51) * mm, "end": v(81.26, -4.72) * mm});
            skPoint(sketch, "E113.visualSharp", {"position": v(60.94, -7.26) * mm});
            skArc(sketch, "E113.filletArc", {"start": v(60.94, -4.72) * mm, "mid": v(61.69, -6.51) * mm, "end": v(63.48, -7.26) * mm});
            skCircle(sketch, "E114", {"center": v(91.42, 61.32) * mm, "radius": 6.35 * mm});
            skSolve(sketch);
        }
        {
            var Q0;
            Q0 = qSketchRegion(id + "F32", true);
            extrude(context, id + "F33", {"entities" : qUnion([Q0]), "operationType" : NewBodyOperationType.REMOVE, "endBound" : BoundingType.THROUGH_ALL, "oppositeDirection" : true, "depth" : 25.4 * mm});
        }
        {
            var Q0;
            Q0 = qSketchRegion(id + "F27", true);
            extrude(context, id + "F34", {"entities" : qUnion([Q0]), "operationType" : NewBodyOperationType.ADD, "oppositeDirection" : true, "depth" : 1.78 * mm});
        }
        {
            var Q0;
            Q0 = qSketchRegion(id + "F28", true);
            var Q1;
            Q1=sQuery(id+"F28.wireOp",EDGE,"E99");
            extrude(context, id + "F35", {"entities" : qUnion([Q0]), "surfaceEntities" : qUnion([Q1]), "depth" : 15.88 * mm});
        }
    });
